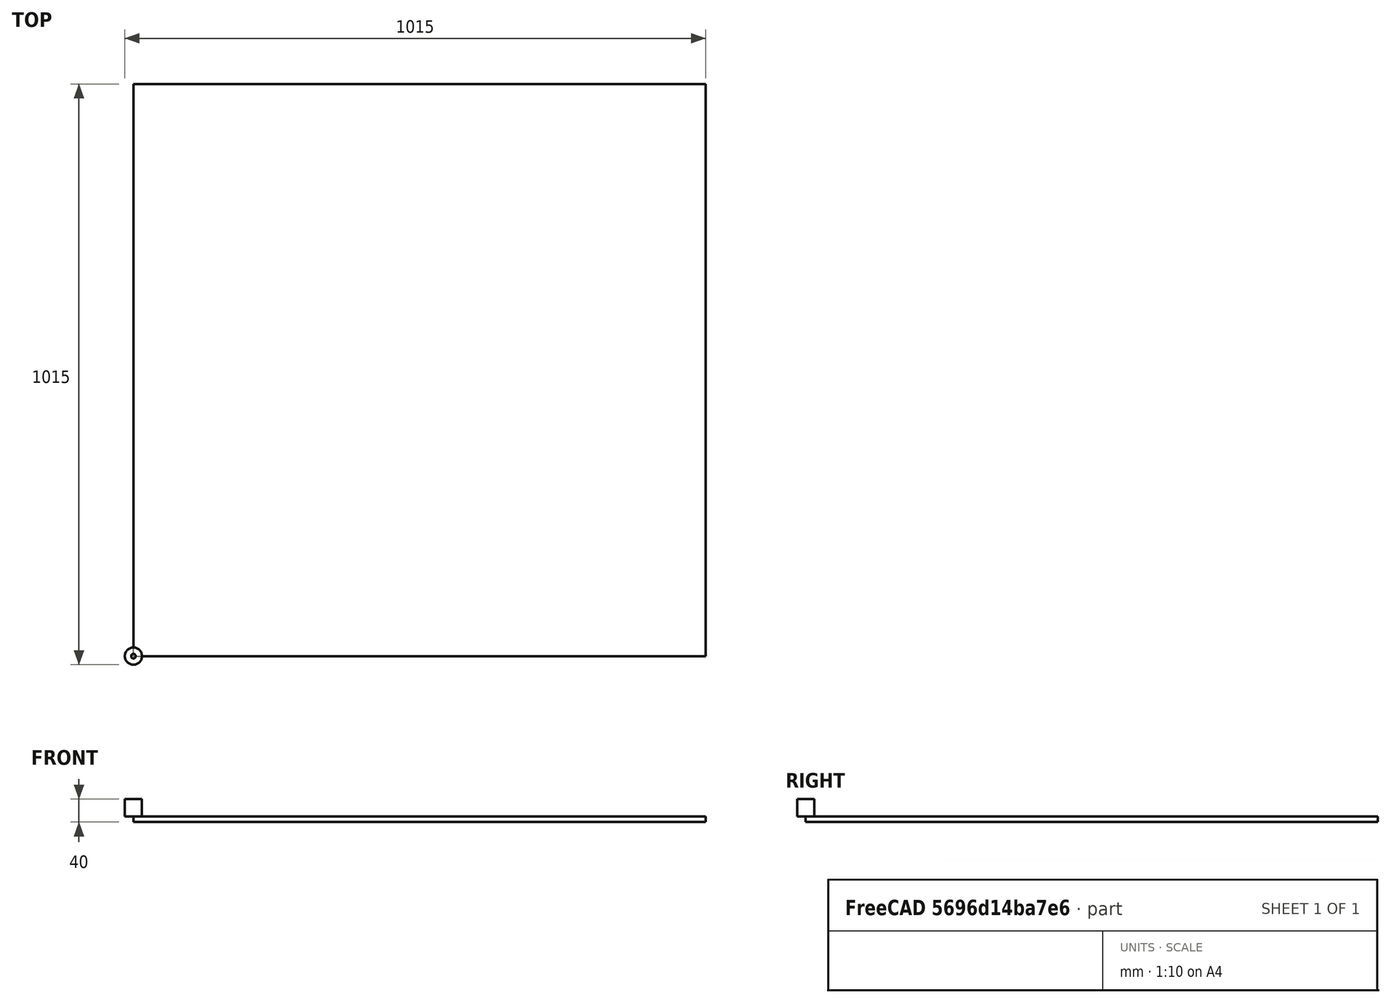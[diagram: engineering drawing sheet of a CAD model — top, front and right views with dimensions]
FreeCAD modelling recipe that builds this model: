
FCSTD DOCUMENT  (FreeCAD 0.19R14555 (Git shallow))
Label: 1mSQPlane
License: All rights reserved
LicenseURL: http://en.wikipedia.org/wiki/All_rights_reserved
objects: Part::FeaturePython×3, Path::FeaturePython×3, App::DocumentObjectGroup×2, Mesh::FeaturePython×2, Sketcher::SketchObject×1, PartDesign::Pad×1, PartDesign::Body×1, App::FeaturePython×1, Path::FeatureCompoundPython×1
note: 8 computed .brp shape members not serialized (recipe doc carries the construction recipe); baked Part::Feature solids carry a one-line shape summary decoded from their .brp

FEATURE [Sketcher::SketchObject] Sketch
  FullyConstrained = true
  MapMode = 5
  Support = -> [XY_Plane]
  sketch-geometry (4):
    g0: LineSegment StartX=-500 StartY=500 StartZ=0 EndX=500 EndY=500 EndZ=0
    g1: LineSegment StartX=500 StartY=500 StartZ=0 EndX=500 EndY=-500 EndZ=0
    g2: LineSegment StartX=500 StartY=-500 StartZ=0 EndX=-500 EndY=-500 EndZ=0
    g3: LineSegment StartX=-500 StartY=-500 StartZ=0 EndX=-500 EndY=500 EndZ=0
  constraints (12):
    c: Coincident(g0,g1)
    c: Coincident(g1,g2)
    c: Coincident(g2,g3)
    c: Coincident(g3,g0)
    c: Horizontal(g0)
    c: Horizontal(g2)
    c: Vertical(g1)
    c: Vertical(g3)
    c: DistanceX(g0,g0) = 1000
    c: DistanceY(g3,g3) = 1000
    c: DistanceY(g-1,g0) = 500
    c: DistanceX(g-1,g0) = 500
FEATURE [PartDesign::Pad] Pad
  Direction = (1,1,1)
  Length = 10
  Length2 = 100
  Profile = -> Sketch
  Type = 0
FEATURE [PartDesign::Body] Body
  Group = -> [Sketch,Pad]
  Origin = -> Origin
  Tip = -> Pad
FEATURE [App::FeaturePython] SetupSheet  # Path/CAM operation (typed FeaturePython)
  ClearanceHeightExpression = OpStockZMax+SetupSheet.ClearanceHeightOffset
  ClearanceHeightOffset = 5
  CoolantMode = 0
  CoolantModes = None | Flood | Mist
  FinalDepthExpression = OpFinalDepth
  HorizRapid = 0
  SafeHeightExpression = OpStockZMax+SetupSheet.SafeHeightOffset
  SafeHeightOffset = 3
  StartDepthExpression = OpStartDepth
  StepDownExpression = OpToolDiameter
  VertRapid = 0
FEATURE [Part::FeaturePython] Clone  label="Model-Body"  # Draft clone (typed FeaturePython)
  AttacherType = Attacher::AttachEngine3D
  Fuse = false
  Objects = -> [Body]
  PathResource = Model
  Placement = pos=(500,500,-10) rot=(0,0,1;0rad)
  Scale = (1,1,1)
FEATURE [App::DocumentObjectGroup] Model
  Group = -> [Clone]
FEATURE [Part::FeaturePython] ToolBit001  label="Planing Endmill"  # Path/CAM toolbit (typed FeaturePython)
  BitPropertyNames = Chipload | CuttingEdgeHeight | Diameter | Flutes | Length | Material | ShankDiameter
  BitShape = /app/freecad/Mod/Path/Tools/Shape/endmill.fcstd
  Chipload = 0
  CuttingEdgeHeight = 30
  Diameter = 30
  File = <userpath>/Documents/MensShed/FreeCAD/Bit/PlaningEndmill.fctb
  Flutes = 0
  Length = 30
  Material = 0
  ShankDiameter = 8
  ShapeName = endmill
FEATURE [Path::FeaturePython] Planing_Endmill  label="Planing Endmill001"  # Path/CAM operation (typed FeaturePython)
  HorizFeed = 10
  HorizRapid = 0
  SpindleDir = 0
  SpindleSpeed = 2000
  Tool = -> ToolBit001
  ToolNumber = 1
  VertFeed = 10
  VertRapid = 0
  expr: VertRapid = SetupSheet.VertRapid
  expr: HorizRapid = SetupSheet.HorizRapid
FEATURE [App::DocumentObjectGroup] Tools
  Group = -> [Planing_Endmill]
FEATURE [Part::FeaturePython] Stock001  # WARN: FeaturePython — macro-defined, semantics opaque (R4)
  Height = 10
  Length = 1000
  Placement = pos=(0,0,-10) rot=(0,0,1;0rad)
  StockType = CreateBox
  Width = 1000
FEATURE [Path::FeaturePython] MillFace  # Path/CAM operation (typed FeaturePython)
  Active = true
  AreaParams:
    Tolerance = 1e-07
    FitArcs = True
    Simplify = False
    CleanDistance = 0.0
    Accuracy = 0.01
    Unit = 1.0
    MinArcPoints = 4
    MaxArcPoints = 100
    ClipperScale = 10000000.0
    Fill = 0
    Coplanar = 0
    Reorient = True
    Outline = False
    Explode = False
    OpenMode = 0
    Deflection = 0.01
    SubjectFill = 0
    ClipFill = 0
    Offset = 0.0
    ExtraPass = 0
    Stepover = 0.0
    LastStepover = 0.0
    JoinType = 0
    EndType = 0
    MiterLimit = 2.0
    RoundPrecision = 0.0
    PocketMode = 1
    ToolRadius = 15.0
    PocketExtraOffset = 0.0
    PocketStepover = 15.0
    PocketLastStepover = 0.0
    FromCenter = True
    Angle = 45.0
    AngleShift = 0.0
    Shift = 0.0
    Thicken = False
    SectionCount = -1
    Stepdown = 1.0
    SectionOffset = 0.0
    SectionTolerance = 1e-06
    SectionMode = 2
    Project = False
  Base = -> [Clone]
  BoundaryShape = 0
  ClearEdges = false
  ClearanceHeight = 5
  CoolantMode = Mist
  CutMode = 1
  CycleTime = 03:37:14
  EnableRotation = 0
  ExcludeRaisedAreas = false
  ExtraOffset = 0
  FinalDepth = 0
  FinishDepth = 1
  KeepToolDown = false
  MinTravel = false
  OffsetPattern = 0
  OpFinalDepth = 0
  OpStartDepth = 30
  OpStockZMax = 0
  OpStockZMin = -10
  OpToolDiameter = 30
  PathParams = {'orientation': 0, 'feedrate': 10.0, 'feedrate_v': 10.0, 'verbose': True, 'resume_height': 3.0, 'retraction': 5.0, 'return_end': True, 'preamble': False}
  SafeHeight = 3
  StartAt = 0
  StartDepth = 30
  StartPoint = (0,0,0)
  StepDown = 30
  StepOver = 50
  ToolController = -> Planing_Endmill
  UseStartPoint = false
  ZigZagAngle = 45
  expr: StartDepth = OpStartDepth
  expr: FinalDepth = OpFinalDepth
  expr: StepDown = OpToolDiameter
  expr: SafeHeight = OpStockZMax + SetupSheet.SafeHeightOffset
  expr: ClearanceHeight = OpStockZMax + SetupSheet.ClearanceHeightOffset
FEATURE [Path::FeatureCompoundPython] Operations  # Path/CAM operation (typed FeaturePython)
  Group = -> [MillFace]
  UsePlacements = false
FEATURE [Path::FeaturePython] Job  # Path/CAM operation (typed FeaturePython)
  CycleTime = 03:37:14
  GeometryTolerance = 0.01
  LastPostProcessDate = 2021-12-01 08:22:30.169755
  LastPostProcessOutput = <userpath>/Documents/MensShed/1mSQPlane1.ngc
  Model = -> Model
  Operations = -> Operations
  OrderOutputBy = 0
  PostProcessor = 7
  PostProcessorOutputFile = <userpath>/Documents/MensShed/1mSQPlane1.ngc
  SetupSheet = -> SetupSheet
  SplitOutput = false
  Stock = -> Stock001
  Tools = -> Tools
FEATURE [Mesh::FeaturePython] CutMaterial  # WARN: FeaturePython — macro-defined, semantics opaque (R4)
FEATURE [Mesh::FeaturePython] CutMaterial001  # WARN: FeaturePython — macro-defined, semantics opaque (R4)
